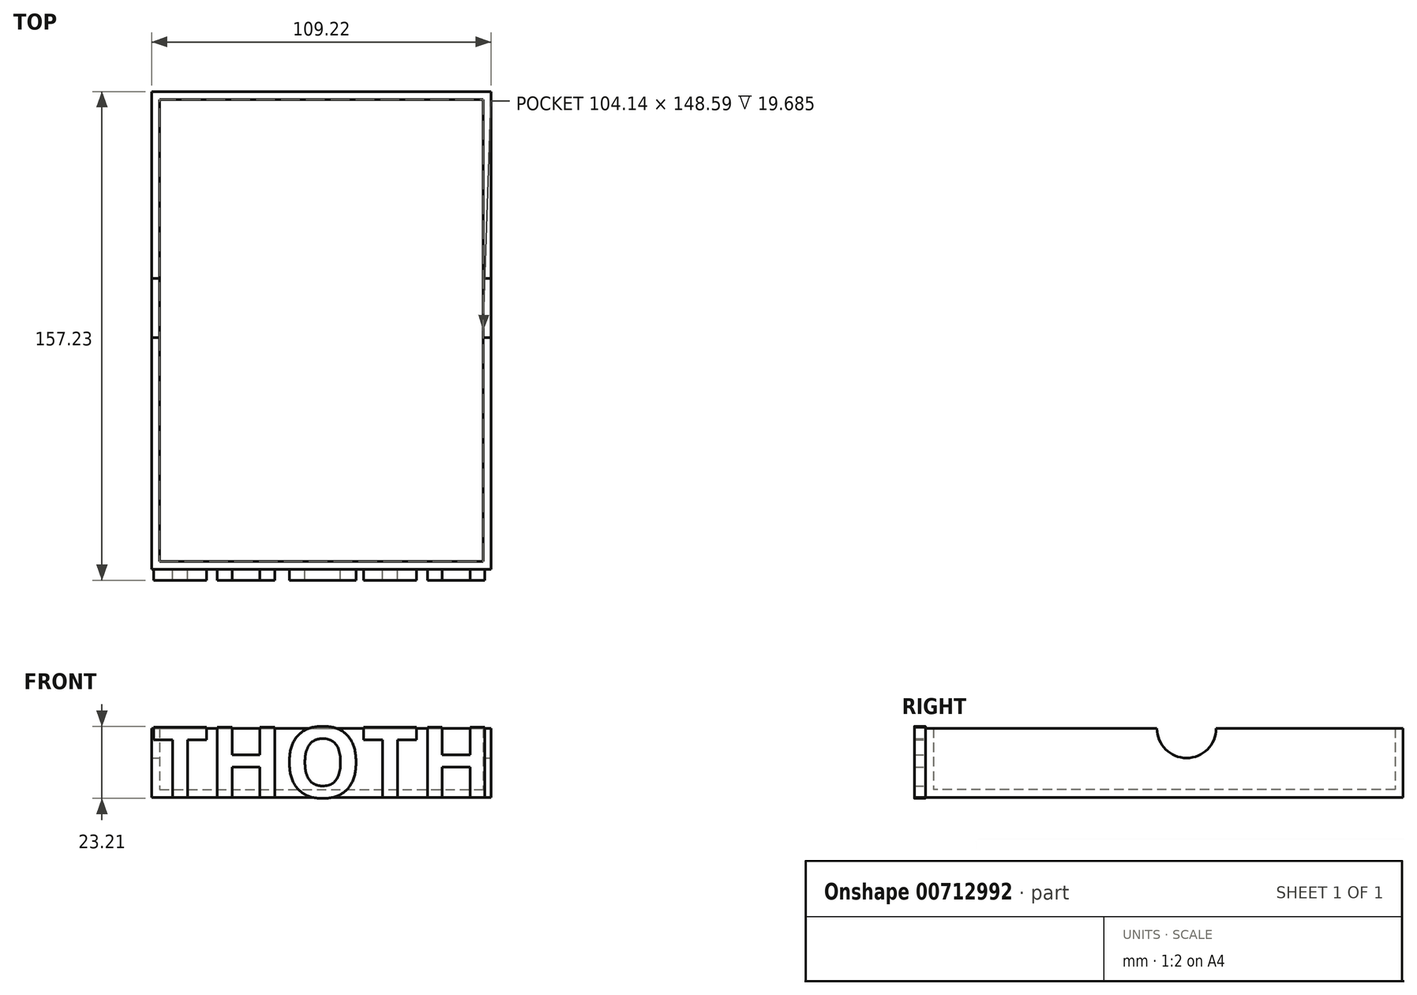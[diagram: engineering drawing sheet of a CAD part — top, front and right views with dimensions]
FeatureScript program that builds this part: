
annotation { "Feature Type Name" : "Feature", "Feature Type Description" : "" }
export const myFeature = defineFeature(function(context is Context, id is Id, definition is map)
    precondition{}
    {
        {
            var Q0;
            Q0=qCreatedBy(makeId("Top.planeOp"),FACE);
            var sketch = newSketch(context, id + "F0", { "sketchPlane" : qUnion([Q0])});
            skLineSegment(sketch, "E0.bottom", {"start": v(-64.26, 69.64) * mm, "end": v(44.96, 69.64) * mm});
            skLineSegment(sketch, "E0.top", {"start": v(-64.26, -84.03) * mm, "end": v(44.96, -84.03) * mm});
            skLineSegment(sketch, "E0.left", {"start": v(-64.26, 69.64) * mm, "end": v(-64.26, -84.03) * mm});
            skLineSegment(sketch, "E0.right", {"start": v(44.96, 69.64) * mm, "end": v(44.96, -84.03) * mm});
            skSolve(sketch);
        }
        {
            var Q0;
            Q0=makeQuery(id+"F0.imprint","IMPRINT",FACE,{"disambiguationData":[TD([[makeQuery(id+"F0.imprint","IMPRINT",EDGE,{"derivedFrom":sQuery(id+"F0.wireOp",EDGE,"E0.bottom")}),-1.0]])]});
            extrude(context, id + "F1", {"entities" : qUnion([Q0]), "depth" : 22.22 * mm, "offsetDistance" : 25.4 * mm});
        }
        {
            var Q0;
            Q0=makeQuery(id+"F1.opExtrude","CAP_FACE",FACE,{"disambiguationData":[OSD([sQuery(id+"F0.wireOp",EDGE,"E0.bottom"),sQuery(id+"F0.wireOp",EDGE,"E0.top"),sQuery(id+"F0.wireOp",EDGE,"E0.left"),sQuery(id+"F0.wireOp",EDGE,"E0.right")])],"isStart":false});
            shell(context, id + "F2", {"entities" : qUnion([Q0]), "thickness" : 2.54 * mm});
        }
        {
            var Q0;
            Q0=makeQuery(id+"F1.opExtrude","SWEPT_FACE",FACE,{"disambiguationData":[OSD([sQuery(id+"F0.wireOp",EDGE,"E0.right")])]});
            var sketch = newSketch(context, id + "F3", { "sketchPlane" : qUnion([Q0])});
            skPoint(sketch, "E1", {"position": v(0, 22.23) * mm});
            skSolve(sketch);
        }
        {
            var Q0;
            Q0=sQuery(id+"F3.wireOp",VERTEX,"E1");
            var Q1;
            Q1=makeQuery(id+"F1.opExtrude","SWEPT_BODY",BODY,{"disambiguationData":[OSD([sQuery(id+"F0.wireOp",EDGE,"E0.bottom"),sQuery(id+"F0.wireOp",EDGE,"E0.top"),sQuery(id+"F0.wireOp",EDGE,"E0.left"),sQuery(id+"F0.wireOp",EDGE,"E0.right")])]});
            hole(context, id + "F4", {"style" : HoleStyle.SIMPLE, "endStyle" : HoleEndStyle.THROUGH, "holeDiameter" : 19.05 * mm, "majorDiameter" : 6.35 * mm, "isTappedThrough" : true, "tappedDepth" : 12.7 * mm, "tapClearance" : 3, "locations" : qUnion([Q0]), "scope" : qUnion([Q1])});
        }
        {
            var Q0;
            Q0=makeQuery(id+"F1.opExtrude","SWEPT_FACE",FACE,{"disambiguationData":[OSD([sQuery(id+"F0.wireOp",EDGE,"E0.top")])]});
            var sketch = newSketch(context, id + "F5", { "sketchPlane" : qUnion([Q0])});
            skText(sketch, "E2", { "text": "THOTH\n", "fontName": "OpenSans-Bold.ttf"});
            const initialGuessF5  = {"E2": [-0.06426, 0, 1, 0, 0.02274]};
            skSetInitialGuess(sketch, initialGuessF5);
            skSolve(sketch);
        }
        {
            var Q0;
            Q0 = qSketchRegion(id + "F5", true);
            extrude(context, id + "F6", {"entities" : qUnion([Q0]), "operationType" : NewBodyOperationType.ADD, "depth" : 3.56 * mm, "offsetDistance" : 25.4 * mm});
        }
    });
